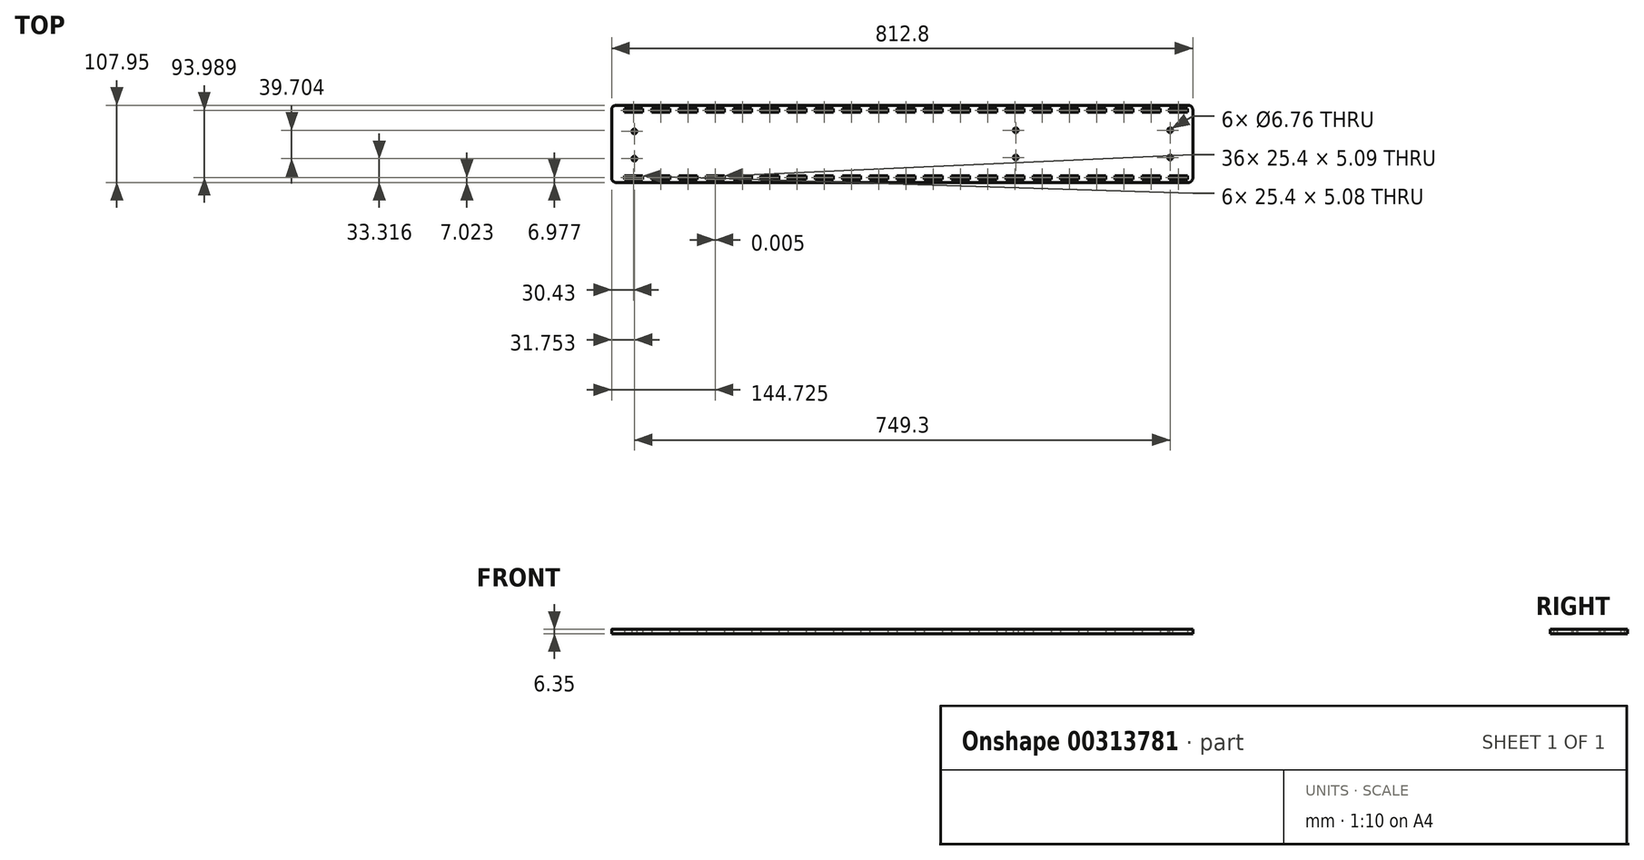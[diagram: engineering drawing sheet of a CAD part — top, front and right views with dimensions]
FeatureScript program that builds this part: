
annotation { "Feature Type Name" : "Feature", "Feature Type Description" : "" }
export const myFeature = defineFeature(function(context is Context, id is Id, definition is map)
    precondition{}
    {
        {
            var Q0;
            Q0=qCreatedBy(makeId("Top.planeOp"),FACE);
            var sketch = newSketch(context, id + "F0", { "sketchPlane" : qUnion([Q0])});
            skPoint(sketch, "E0.middle", {"position": v(-121.33, 38.43) * mm});
            skCircle(sketch, "E1", {"center": v(-278.76, 57.48) * mm, "radius": 3.38 * mm});
            skCircle(sketch, "E2", {"center": v(-62.86, 57.48) * mm, "radius": 3.38 * mm});
            skCircle(sketch, "E3.MirrorC", {"center": v(-278.76, 19.38) * mm, "radius": 3.38 * mm});
            skCircle(sketch, "E4.MirrorC", {"center": v(-62.86, 19.38) * mm, "radius": 3.38 * mm});
            skLineSegment(sketch, "E5", {"start": v(-31.1, 86.06) * mm, "end": v(-31.1, -9.2) * mm});
            skLineSegment(sketch, "E6", {"start": v(-368.98, 87.97) * mm, "end": v(-368.98, 82.89) * mm});
            skLineSegment(sketch, "E7", {"start": v(-368.98, 82.89) * mm, "end": v(-343.58, 82.88) * mm});
            skLineSegment(sketch, "E8", {"start": v(-343.58, 82.88) * mm, "end": v(-343.58, 87.97) * mm});
            skLineSegment(sketch, "E9", {"start": v(-343.58, 87.97) * mm, "end": v(-368.98, 87.97) * mm});
            skLineSegment(sketch, "E10.1.0.0", {"start": v(-330.88, 82.89) * mm, "end": v(-305.48, 82.88) * mm});
            skLineSegment(sketch, "E10.1.0.1", {"start": v(-305.48, 87.97) * mm, "end": v(-330.88, 87.97) * mm});
            skLineSegment(sketch, "E10.1.0.2", {"start": v(-330.88, 87.97) * mm, "end": v(-330.88, 82.89) * mm});
            skLineSegment(sketch, "E10.1.0.3", {"start": v(-305.48, 82.88) * mm, "end": v(-305.48, 87.97) * mm});
            skLineSegment(sketch, "E10.2.0.0", {"start": v(-292.78, 82.89) * mm, "end": v(-267.38, 82.88) * mm});
            skLineSegment(sketch, "E10.2.0.1", {"start": v(-267.38, 87.97) * mm, "end": v(-292.78, 87.97) * mm});
            skLineSegment(sketch, "E10.2.0.2", {"start": v(-292.78, 87.97) * mm, "end": v(-292.78, 82.89) * mm});
            skLineSegment(sketch, "E10.2.0.3", {"start": v(-267.38, 82.88) * mm, "end": v(-267.38, 87.97) * mm});
            skLineSegment(sketch, "E10.3.0.0", {"start": v(-254.68, 82.89) * mm, "end": v(-229.28, 82.88) * mm});
            skLineSegment(sketch, "E10.3.0.1", {"start": v(-229.28, 87.97) * mm, "end": v(-254.68, 87.97) * mm});
            skLineSegment(sketch, "E10.3.0.2", {"start": v(-254.68, 87.97) * mm, "end": v(-254.68, 82.89) * mm});
            skLineSegment(sketch, "E10.3.0.3", {"start": v(-229.28, 82.88) * mm, "end": v(-229.28, 87.97) * mm});
            skLineSegment(sketch, "E10.4.0.0", {"start": v(-216.58, 82.89) * mm, "end": v(-191.18, 82.88) * mm});
            skLineSegment(sketch, "E10.4.0.1", {"start": v(-191.18, 87.97) * mm, "end": v(-216.58, 87.97) * mm});
            skLineSegment(sketch, "E10.4.0.2", {"start": v(-216.58, 87.97) * mm, "end": v(-216.58, 82.89) * mm});
            skLineSegment(sketch, "E10.4.0.3", {"start": v(-191.18, 82.88) * mm, "end": v(-191.18, 87.97) * mm});
            skLineSegment(sketch, "E10.5.0.0", {"start": v(-178.48, 82.89) * mm, "end": v(-153.08, 82.88) * mm});
            skLineSegment(sketch, "E10.5.0.1", {"start": v(-153.08, 87.97) * mm, "end": v(-178.48, 87.97) * mm});
            skLineSegment(sketch, "E10.5.0.2", {"start": v(-178.48, 87.97) * mm, "end": v(-178.48, 82.89) * mm});
            skLineSegment(sketch, "E10.5.0.3", {"start": v(-153.08, 82.88) * mm, "end": v(-153.08, 87.97) * mm});
            skLineSegment(sketch, "E10.6.0.0", {"start": v(-140.38, 82.89) * mm, "end": v(-114.98, 82.88) * mm});
            skLineSegment(sketch, "E10.6.0.1", {"start": v(-114.98, 87.97) * mm, "end": v(-140.38, 87.97) * mm});
            skLineSegment(sketch, "E10.6.0.2", {"start": v(-140.38, 87.97) * mm, "end": v(-140.38, 82.89) * mm});
            skLineSegment(sketch, "E10.6.0.3", {"start": v(-114.98, 82.88) * mm, "end": v(-114.98, 87.97) * mm});
            skLineSegment(sketch, "E10.7.0.0", {"start": v(-102.28, 82.89) * mm, "end": v(-76.88, 82.88) * mm});
            skLineSegment(sketch, "E10.7.0.1", {"start": v(-76.88, 87.97) * mm, "end": v(-102.28, 87.97) * mm});
            skLineSegment(sketch, "E10.7.0.2", {"start": v(-102.28, 87.97) * mm, "end": v(-102.28, 82.89) * mm});
            skLineSegment(sketch, "E10.7.0.3", {"start": v(-76.88, 82.88) * mm, "end": v(-76.88, 87.97) * mm});
            skLineSegment(sketch, "E10.8.0.0", {"start": v(-64.18, 82.89) * mm, "end": v(-38.78, 82.88) * mm});
            skLineSegment(sketch, "E10.8.0.1", {"start": v(-38.78, 87.97) * mm, "end": v(-64.18, 87.97) * mm});
            skLineSegment(sketch, "E10.8.0.2", {"start": v(-64.18, 87.97) * mm, "end": v(-64.18, 82.89) * mm});
            skLineSegment(sketch, "E10.8.0.3", {"start": v(-38.78, 82.88) * mm, "end": v(-38.78, 87.97) * mm});
            skLineSegment(sketch, "E11", {"start": v(-381.68, 38.44) * mm, "end": v(-270.62, 38.43) * mm});
            skPoint(sketch, "E11.endSnap0", {"position": v(-381.68, 38.43) * mm});
            skLineSegment(sketch, "E12.MirrorCS", {"start": v(-140.38, -11.12) * mm, "end": v(-140.39, -6.04) * mm});
            skLineSegment(sketch, "E13.MirrorCS", {"start": v(-64.18, -11.12) * mm, "end": v(-64.19, -6.04) * mm});
            skLineSegment(sketch, "E14.MirrorCS", {"start": v(-216.58, -11.1) * mm, "end": v(-216.59, -6.03) * mm});
            skLineSegment(sketch, "E15.MirrorCS", {"start": v(-267.38, -6.02) * mm, "end": v(-267.38, -11.1) * mm});
            skLineSegment(sketch, "E16.MirrorCS", {"start": v(-114.98, -6.03) * mm, "end": v(-114.98, -11.12) * mm});
            skLineSegment(sketch, "E17.MirrorCS", {"start": v(-330.88, -11.1) * mm, "end": v(-330.89, -6.02) * mm});
            skLineSegment(sketch, "E18.MirrorCS", {"start": v(-305.48, -6.01) * mm, "end": v(-305.48, -11.1) * mm});
            skLineSegment(sketch, "E19.MirrorCS", {"start": v(-153.08, -6.03) * mm, "end": v(-153.08, -11.12) * mm});
            skLineSegment(sketch, "E20.MirrorCS", {"start": v(-368.98, -11.1) * mm, "end": v(-368.99, -6.01) * mm});
            skLineSegment(sketch, "E21.MirrorCS", {"start": v(-191.18, -6.02) * mm, "end": v(-191.18, -11.11) * mm});
            skLineSegment(sketch, "E22.MirrorCS", {"start": v(-38.78, -6.04) * mm, "end": v(-38.78, -11.13) * mm});
            skLineSegment(sketch, "E23.MirrorCS", {"start": v(-76.88, -6.04) * mm, "end": v(-76.88, -11.12) * mm});
            skLineSegment(sketch, "E24.MirrorCS", {"start": v(-292.78, -11.1) * mm, "end": v(-292.79, -6.02) * mm});
            skLineSegment(sketch, "E25.MirrorCS", {"start": v(-254.68, -11.1) * mm, "end": v(-254.69, -6.02) * mm});
            skLineSegment(sketch, "E26.MirrorCS", {"start": v(-102.28, -11.12) * mm, "end": v(-102.29, -6.04) * mm});
            skLineSegment(sketch, "E27.MirrorCS", {"start": v(-229.28, -6.02) * mm, "end": v(-229.28, -11.1) * mm});
            skLineSegment(sketch, "E28.MirrorCS", {"start": v(-343.58, -6) * mm, "end": v(-343.58, -11.1) * mm});
            skLineSegment(sketch, "E29.MirrorCS", {"start": v(-178.48, -11.11) * mm, "end": v(-178.49, -6.03) * mm});
            skLineSegment(sketch, "E30.MirrorCS", {"start": v(-368.99, -6.01) * mm, "end": v(-343.58, -6) * mm});
            skLineSegment(sketch, "E31.MirrorCS", {"start": v(-305.48, -11.1) * mm, "end": v(-330.88, -11.1) * mm});
            skLineSegment(sketch, "E32.MirrorCS", {"start": v(-330.89, -6.02) * mm, "end": v(-305.48, -6.01) * mm});
            skLineSegment(sketch, "E33.MirrorCS", {"start": v(-254.69, -6.02) * mm, "end": v(-229.28, -6.02) * mm});
            skLineSegment(sketch, "E34.MirrorCS", {"start": v(-102.29, -6.04) * mm, "end": v(-76.88, -6.04) * mm});
            skLineSegment(sketch, "E35.MirrorCS", {"start": v(-343.58, -11.1) * mm, "end": v(-368.98, -11.1) * mm});
            skLineSegment(sketch, "E36.MirrorCS", {"start": v(-114.98, -11.12) * mm, "end": v(-140.38, -11.12) * mm});
            skLineSegment(sketch, "E37.MirrorCS", {"start": v(-267.38, -11.1) * mm, "end": v(-292.78, -11.1) * mm});
            skLineSegment(sketch, "E38.MirrorCS", {"start": v(-229.28, -11.1) * mm, "end": v(-254.68, -11.1) * mm});
            skLineSegment(sketch, "E39.MirrorCS", {"start": v(-64.19, -6.04) * mm, "end": v(-38.78, -6.04) * mm});
            skLineSegment(sketch, "E40.MirrorCS", {"start": v(-38.78, -11.13) * mm, "end": v(-64.18, -11.12) * mm});
            skLineSegment(sketch, "E41.MirrorCS", {"start": v(-191.18, -11.11) * mm, "end": v(-216.58, -11.1) * mm});
            skLineSegment(sketch, "E42.MirrorCS", {"start": v(-292.79, -6.02) * mm, "end": v(-267.38, -6.02) * mm});
            skLineSegment(sketch, "E43.MirrorCS", {"start": v(-153.08, -11.12) * mm, "end": v(-178.48, -11.11) * mm});
            skLineSegment(sketch, "E44.MirrorCS", {"start": v(-140.39, -6.04) * mm, "end": v(-114.98, -6.03) * mm});
            skLineSegment(sketch, "E45.MirrorCS", {"start": v(-368.99, -6.01) * mm, "end": v(-330.89, -6.02) * mm, "construction": true});
            skLineSegment(sketch, "E46.MirrorCS", {"start": v(-178.49, -6.03) * mm, "end": v(-153.08, -6.03) * mm});
            skLineSegment(sketch, "E47.MirrorCS", {"start": v(-216.59, -6.03) * mm, "end": v(-191.18, -6.02) * mm});
            skLineSegment(sketch, "E48.MirrorCS", {"start": v(-76.88, -11.12) * mm, "end": v(-102.28, -11.12) * mm});
            skCircle(sketch, "E49", {"center": v(-812.16, 55.88) * mm, "radius": 3.38 * mm});
            skCircle(sketch, "E50", {"center": v(-812.16, 17.78) * mm, "radius": 3.38 * mm});
            skPoint(sketch, "E51.endSnap0", {"position": v(-165.78, 87.97) * mm});
            skLineSegment(sketch, "E52", {"start": v(-37.46, -15.54) * mm, "end": v(-837.56, -15.54) * mm});
            skLineSegment(sketch, "E53", {"start": v(-843.9, -9.2) * mm, "end": v(-843.9, 86.06) * mm});
            skLineSegment(sketch, "E54", {"start": v(-837.56, 92.4) * mm, "end": v(-37.46, 92.4) * mm});
            skLineSegment(sketch, "E55.1.0.0", {"start": v(-381.68, 87.97) * mm, "end": v(-407.08, 87.97) * mm});
            skLineSegment(sketch, "E55.1.0.1", {"start": v(-407.08, 87.97) * mm, "end": v(-407.08, 82.89) * mm});
            skLineSegment(sketch, "E55.1.0.2", {"start": v(-381.68, 82.88) * mm, "end": v(-381.68, 87.97) * mm});
            skLineSegment(sketch, "E55.2.0.0", {"start": v(-419.78, 87.97) * mm, "end": v(-445.18, 87.97) * mm});
            skLineSegment(sketch, "E55.2.0.1", {"start": v(-445.18, 87.97) * mm, "end": v(-445.18, 82.89) * mm});
            skLineSegment(sketch, "E55.2.0.2", {"start": v(-419.78, 82.88) * mm, "end": v(-419.78, 87.97) * mm});
            skLineSegment(sketch, "E55.3.0.0", {"start": v(-457.88, 87.97) * mm, "end": v(-483.28, 87.97) * mm});
            skLineSegment(sketch, "E55.3.0.1", {"start": v(-483.28, 87.97) * mm, "end": v(-483.28, 82.89) * mm});
            skLineSegment(sketch, "E55.3.0.2", {"start": v(-457.88, 82.88) * mm, "end": v(-457.88, 87.97) * mm});
            skLineSegment(sketch, "E55.4.0.0", {"start": v(-495.98, 87.97) * mm, "end": v(-521.38, 87.97) * mm});
            skLineSegment(sketch, "E55.4.0.1", {"start": v(-521.38, 87.97) * mm, "end": v(-521.38, 82.89) * mm});
            skLineSegment(sketch, "E55.4.0.2", {"start": v(-495.98, 82.88) * mm, "end": v(-495.98, 87.97) * mm});
            skLineSegment(sketch, "E55.5.0.0", {"start": v(-534.08, 87.97) * mm, "end": v(-559.48, 87.97) * mm});
            skLineSegment(sketch, "E55.5.0.1", {"start": v(-559.48, 87.97) * mm, "end": v(-559.48, 82.89) * mm});
            skLineSegment(sketch, "E55.5.0.2", {"start": v(-534.08, 82.88) * mm, "end": v(-534.08, 87.97) * mm});
            skLineSegment(sketch, "E55.6.0.0", {"start": v(-572.18, 87.97) * mm, "end": v(-597.58, 87.97) * mm});
            skLineSegment(sketch, "E55.6.0.1", {"start": v(-597.58, 87.97) * mm, "end": v(-597.58, 82.89) * mm});
            skLineSegment(sketch, "E55.6.0.2", {"start": v(-572.18, 82.88) * mm, "end": v(-572.18, 87.97) * mm});
            skLineSegment(sketch, "E55.7.0.0", {"start": v(-610.28, 87.97) * mm, "end": v(-635.68, 87.97) * mm});
            skLineSegment(sketch, "E55.7.0.1", {"start": v(-635.68, 87.97) * mm, "end": v(-635.68, 82.89) * mm});
            skLineSegment(sketch, "E55.7.0.2", {"start": v(-610.28, 82.88) * mm, "end": v(-610.28, 87.97) * mm});
            skLineSegment(sketch, "E55.8.0.0", {"start": v(-648.38, 87.97) * mm, "end": v(-673.78, 87.97) * mm});
            skLineSegment(sketch, "E55.8.0.1", {"start": v(-673.78, 87.97) * mm, "end": v(-673.78, 82.89) * mm});
            skLineSegment(sketch, "E55.8.0.2", {"start": v(-648.38, 82.88) * mm, "end": v(-648.38, 87.97) * mm});
            skLineSegment(sketch, "E55.9.0.0", {"start": v(-686.48, 87.97) * mm, "end": v(-711.88, 87.97) * mm});
            skLineSegment(sketch, "E55.9.0.1", {"start": v(-711.88, 87.97) * mm, "end": v(-711.88, 82.89) * mm});
            skLineSegment(sketch, "E55.9.0.2", {"start": v(-686.48, 82.88) * mm, "end": v(-686.48, 87.97) * mm});
            skLineSegment(sketch, "E55.10.0.0", {"start": v(-724.58, 87.97) * mm, "end": v(-749.98, 87.97) * mm});
            skLineSegment(sketch, "E55.10.0.1", {"start": v(-749.98, 87.97) * mm, "end": v(-749.98, 82.89) * mm});
            skLineSegment(sketch, "E55.10.0.2", {"start": v(-724.58, 82.88) * mm, "end": v(-724.58, 87.97) * mm});
            skLineSegment(sketch, "E55.11.0.0", {"start": v(-762.68, 87.97) * mm, "end": v(-788.08, 87.97) * mm});
            skLineSegment(sketch, "E55.11.0.1", {"start": v(-788.08, 87.97) * mm, "end": v(-788.08, 82.89) * mm});
            skLineSegment(sketch, "E55.11.0.2", {"start": v(-762.68, 82.88) * mm, "end": v(-762.68, 87.97) * mm});
            skLineSegment(sketch, "E56", {"start": v(-788.08, 82.89) * mm, "end": v(-762.68, 82.89) * mm});
            skLineSegment(sketch, "E57.trimOffspring", {"start": v(-749.98, 82.89) * mm, "end": v(-724.58, 82.89) * mm});
            skLineSegment(sketch, "E58", {"start": v(-419.78, 82.88) * mm, "end": v(-445.18, 82.89) * mm});
            skLineSegment(sketch, "E59", {"start": v(-457.88, 82.88) * mm, "end": v(-483.28, 82.89) * mm});
            skLineSegment(sketch, "E60", {"start": v(-495.98, 82.88) * mm, "end": v(-521.38, 82.89) * mm});
            skLineSegment(sketch, "E61", {"start": v(-534.08, 82.88) * mm, "end": v(-559.48, 82.89) * mm});
            skLineSegment(sketch, "E62", {"start": v(-572.18, 82.88) * mm, "end": v(-597.58, 82.89) * mm});
            skLineSegment(sketch, "E63", {"start": v(-610.28, 82.88) * mm, "end": v(-635.68, 82.89) * mm});
            skLineSegment(sketch, "E64", {"start": v(-648.38, 82.88) * mm, "end": v(-673.78, 82.89) * mm});
            skLineSegment(sketch, "E65", {"start": v(-686.48, 82.88) * mm, "end": v(-711.88, 82.89) * mm});
            skLineSegment(sketch, "E66", {"start": v(-381.68, 82.88) * mm, "end": v(-407.08, 82.89) * mm});
            skLineSegment(sketch, "E67.MirrorCS", {"start": v(-711.88, -11.06) * mm, "end": v(-711.89, -5.98) * mm});
            skLineSegment(sketch, "E68.MirrorCS", {"start": v(-648.38, -5.98) * mm, "end": v(-648.38, -11.06) * mm});
            skLineSegment(sketch, "E69.MirrorCS", {"start": v(-724.58, -5.97) * mm, "end": v(-724.58, -11.06) * mm});
            skLineSegment(sketch, "E70.MirrorCS", {"start": v(-673.78, -11.06) * mm, "end": v(-673.79, -5.98) * mm});
            skLineSegment(sketch, "E71.MirrorCS", {"start": v(-749.98, -11.05) * mm, "end": v(-749.99, -5.97) * mm});
            skLineSegment(sketch, "E72.MirrorCS", {"start": v(-788.08, -11.05) * mm, "end": v(-788.09, -5.97) * mm});
            skLineSegment(sketch, "E73.MirrorCS", {"start": v(-686.48, -5.97) * mm, "end": v(-686.48, -11.06) * mm});
            skLineSegment(sketch, "E74.MirrorCS", {"start": v(-762.68, -5.97) * mm, "end": v(-762.68, -11.05) * mm});
            skLineSegment(sketch, "E75.MirrorCS", {"start": v(-597.58, -11.07) * mm, "end": v(-597.59, -5.99) * mm});
            skLineSegment(sketch, "E76.MirrorCS", {"start": v(-572.18, -5.99) * mm, "end": v(-572.18, -11.07) * mm});
            skLineSegment(sketch, "E77.MirrorCS", {"start": v(-635.68, -11.07) * mm, "end": v(-635.69, -5.99) * mm});
            skLineSegment(sketch, "E78.MirrorCS", {"start": v(-610.28, -5.98) * mm, "end": v(-610.28, -11.07) * mm});
            skLineSegment(sketch, "E79.MirrorCS", {"start": v(-762.68, -11.05) * mm, "end": v(-788.08, -11.05) * mm});
            skLineSegment(sketch, "E80.MirrorCS", {"start": v(-648.38, -5.98) * mm, "end": v(-673.79, -5.98) * mm});
            skLineSegment(sketch, "E81.MirrorCS", {"start": v(-572.18, -5.99) * mm, "end": v(-597.59, -5.99) * mm});
            skLineSegment(sketch, "E82.MirrorCS", {"start": v(-610.28, -5.98) * mm, "end": v(-635.69, -5.99) * mm});
            skLineSegment(sketch, "E83.MirrorCS", {"start": v(-648.38, -11.06) * mm, "end": v(-673.78, -11.06) * mm});
            skLineSegment(sketch, "E84.MirrorCS", {"start": v(-686.48, -5.97) * mm, "end": v(-711.89, -5.98) * mm});
            skLineSegment(sketch, "E85.MirrorCS", {"start": v(-572.18, -11.07) * mm, "end": v(-597.58, -11.07) * mm});
            skLineSegment(sketch, "E86.MirrorCS", {"start": v(-724.58, -11.06) * mm, "end": v(-749.98, -11.05) * mm});
            skLineSegment(sketch, "E87.MirrorCS", {"start": v(-788.09, -5.97) * mm, "end": v(-762.68, -5.97) * mm});
            skLineSegment(sketch, "E88.MirrorCS", {"start": v(-749.99, -5.97) * mm, "end": v(-724.58, -5.98) * mm});
            skLineSegment(sketch, "E89.MirrorCS", {"start": v(-610.28, -11.07) * mm, "end": v(-635.68, -11.07) * mm});
            skLineSegment(sketch, "E90.MirrorCS", {"start": v(-686.48, -11.06) * mm, "end": v(-711.88, -11.06) * mm});
            skLineSegment(sketch, "E91.MirrorCS", {"start": v(-534.08, -5.99) * mm, "end": v(-534.08, -11.08) * mm});
            skLineSegment(sketch, "E92.MirrorCS", {"start": v(-559.48, -11.07) * mm, "end": v(-559.49, -6) * mm});
            skLineSegment(sketch, "E93.MirrorCS", {"start": v(-534.08, -5.99) * mm, "end": v(-559.49, -6) * mm});
            skLineSegment(sketch, "E94.MirrorCS", {"start": v(-457.88, -11.08) * mm, "end": v(-483.28, -11.08) * mm});
            skLineSegment(sketch, "E95.MirrorCS", {"start": v(-381.68, -11.1) * mm, "end": v(-407.08, -11.09) * mm});
            skLineSegment(sketch, "E96.MirrorCS", {"start": v(-483.28, -11.08) * mm, "end": v(-483.29, -6) * mm});
            skLineSegment(sketch, "E97.MirrorCS", {"start": v(-534.08, -11.08) * mm, "end": v(-559.48, -11.07) * mm});
            skLineSegment(sketch, "E98.MirrorCS", {"start": v(-445.18, -11.09) * mm, "end": v(-445.19, -6) * mm});
            skLineSegment(sketch, "E99.MirrorCS", {"start": v(-457.88, -6) * mm, "end": v(-483.29, -6) * mm});
            skLineSegment(sketch, "E100.MirrorCS", {"start": v(-495.98, -6) * mm, "end": v(-521.39, -6) * mm});
            skLineSegment(sketch, "E101.MirrorCS", {"start": v(-419.78, -11.09) * mm, "end": v(-445.18, -11.09) * mm});
            skLineSegment(sketch, "E102.MirrorCS", {"start": v(-419.78, -6) * mm, "end": v(-445.19, -6) * mm});
            skLineSegment(sketch, "E103.MirrorCS", {"start": v(-495.98, -6) * mm, "end": v(-495.98, -11.08) * mm});
            skLineSegment(sketch, "E104.MirrorCS", {"start": v(-381.68, -6) * mm, "end": v(-407.09, -6) * mm});
            skLineSegment(sketch, "E105.MirrorCS", {"start": v(-381.68, -6) * mm, "end": v(-381.68, -11.1) * mm});
            skLineSegment(sketch, "E106.MirrorCS", {"start": v(-419.78, -6) * mm, "end": v(-419.78, -11.09) * mm});
            skLineSegment(sketch, "E107.MirrorCS", {"start": v(-521.38, -11.08) * mm, "end": v(-521.39, -6) * mm});
            skLineSegment(sketch, "E108.MirrorCS", {"start": v(-457.88, -6) * mm, "end": v(-457.88, -11.08) * mm});
            skLineSegment(sketch, "E109.MirrorCS", {"start": v(-495.98, -11.08) * mm, "end": v(-521.38, -11.08) * mm});
            skLineSegment(sketch, "E110.MirrorCS", {"start": v(-407.08, -11.09) * mm, "end": v(-407.09, -6) * mm});
            skPoint(sketch, "E111.visualSharp", {"position": v(-843.9, 92.4) * mm});
            skArc(sketch, "E111.filletArc", {"start": v(-837.56, 92.4) * mm, "mid": v(-842.05, 90.55) * mm, "end": v(-843.9, 86.06) * mm});
            skPoint(sketch, "E112.visualSharp", {"position": v(-843.9, -15.54) * mm});
            skArc(sketch, "E112.filletArc", {"start": v(-843.9, -9.2) * mm, "mid": v(-842.05, -13.68) * mm, "end": v(-837.56, -15.54) * mm});
            skPoint(sketch, "E113.visualSharp", {"position": v(-31.1, 92.4) * mm});
            skArc(sketch, "E113.filletArc", {"start": v(-31.1, 86.06) * mm, "mid": v(-32.97, 90.55) * mm, "end": v(-37.46, 92.4) * mm});
            skPoint(sketch, "E114.visualSharp", {"position": v(-31.1, -15.54) * mm});
            skArc(sketch, "E114.filletArc", {"start": v(-37.46, -15.54) * mm, "mid": v(-32.97, -13.68) * mm, "end": v(-31.1, -9.2) * mm});
            skLineSegment(sketch, "E115.1.0.0", {"start": v(-800.78, 87.97) * mm, "end": v(-826.18, 87.97) * mm});
            skLineSegment(sketch, "E115.1.0.1", {"start": v(-826.18, 82.89) * mm, "end": v(-800.78, 82.89) * mm});
            skLineSegment(sketch, "E115.1.0.2", {"start": v(-826.18, 87.97) * mm, "end": v(-826.18, 82.89) * mm});
            skLineSegment(sketch, "E115.1.0.3", {"start": v(-800.78, 82.88) * mm, "end": v(-800.78, 87.97) * mm});
            skLineSegment(sketch, "E116", {"start": v(-843.9, 38.43) * mm, "end": v(-767.3, 38.43) * mm});
            skLineSegment(sketch, "E117.MirrorCS", {"start": v(-826.18, -6.02) * mm, "end": v(-800.78, -6.02) * mm});
            skLineSegment(sketch, "E118.MirrorCS", {"start": v(-800.78, -11.1) * mm, "end": v(-826.18, -11.1) * mm});
            skLineSegment(sketch, "E119.MirrorCS", {"start": v(-800.78, -6.02) * mm, "end": v(-800.78, -11.1) * mm});
            skLineSegment(sketch, "E120.MirrorCS", {"start": v(-826.18, -11.1) * mm, "end": v(-826.18, -6.02) * mm});
            skSolve(sketch);
        }
        {
            var Q0;
            Q0=makeQuery(id+"F0.imprint","IMPRINT",FACE,{"disambiguationData":[TD([[makeQuery(id+"F0.imprint","IMPRINT",EDGE,{"derivedFrom":sQuery(id+"F0.wireOp",EDGE,"E1")}),-1.0]])]});
            extrude(context, id + "F1", {"entities" : qUnion([Q0]), "depth" : 6.35 * mm});
        }
    });
